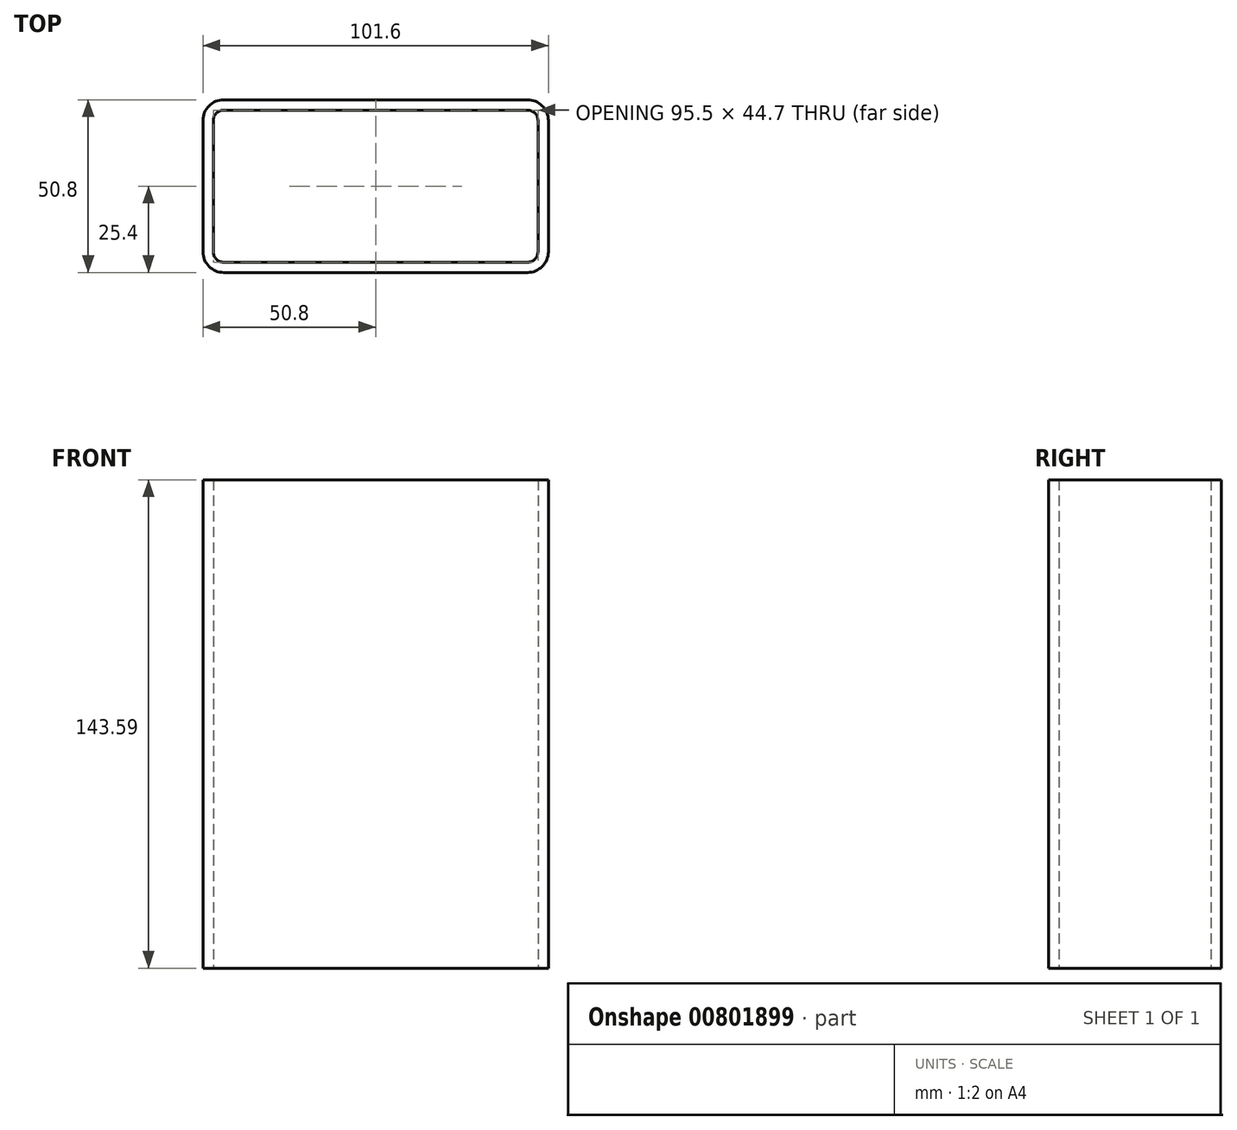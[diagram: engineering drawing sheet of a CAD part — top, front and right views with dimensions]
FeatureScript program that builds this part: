
annotation { "Feature Type Name" : "Feature", "Feature Type Description" : "" }
export const myFeature = defineFeature(function(context is Context, id is Id, definition is map)
    precondition{}
    {
        {
            var Q0;
            Q0=qCreatedBy(makeId("Top.planeOp"),FACE);
            var sketch = newSketch(context, id + "F0", { "sketchPlane" : qUnion([Q0])});
            skLineSegment(sketch, "E0.bottom", {"start": v(6.1, 0) * mm, "end": v(95.5, 0) * mm});
            skLineSegment(sketch, "E0.top", {"start": v(6.1, 50.8) * mm, "end": v(95.5, 50.8) * mm});
            skLineSegment(sketch, "E0.left", {"start": v(0, 6.1) * mm, "end": v(0, 44.7) * mm});
            skLineSegment(sketch, "E0.right", {"start": v(101.6, 6.1) * mm, "end": v(101.6, 44.7) * mm});
            skLineSegment(sketch, "E1.bottom", {"start": v(6.1, 47.75) * mm, "end": v(95.5, 47.75) * mm});
            skLineSegment(sketch, "E1.top", {"start": v(6.1, 3.05) * mm, "end": v(95.5, 3.05) * mm});
            skLineSegment(sketch, "E1.left", {"start": v(3.05, 44.7) * mm, "end": v(3.05, 6.1) * mm});
            skLineSegment(sketch, "E1.right", {"start": v(98.55, 44.7) * mm, "end": v(98.55, 6.1) * mm});
            skPoint(sketch, "E2.visualSharp", {"position": v(3.05, 47.75) * mm});
            skArc(sketch, "E2.filletArc", {"start": v(6.1, 47.75) * mm, "mid": v(3.94, 46.86) * mm, "end": v(3.05, 44.7) * mm});
            skPoint(sketch, "E3.visualSharp", {"position": v(98.55, 47.75) * mm});
            skArc(sketch, "E3.filletArc", {"start": v(98.55, 44.7) * mm, "mid": v(97.66, 46.86) * mm, "end": v(95.5, 47.75) * mm});
            skPoint(sketch, "E4.visualSharp", {"position": v(98.55, 3.05) * mm});
            skArc(sketch, "E4.filletArc", {"start": v(95.5, 3.05) * mm, "mid": v(97.66, 3.94) * mm, "end": v(98.55, 6.1) * mm});
            skPoint(sketch, "E5.visualSharp", {"position": v(3.05, 3.05) * mm});
            skArc(sketch, "E5.filletArc", {"start": v(3.05, 6.1) * mm, "mid": v(3.94, 3.94) * mm, "end": v(6.1, 3.05) * mm});
            skPoint(sketch, "E6.visualSharp", {"position": v(0, 50.8) * mm});
            skArc(sketch, "E6.filletArc", {"start": v(6.1, 50.8) * mm, "mid": v(1.79, 49.01) * mm, "end": v(0, 44.7) * mm});
            skPoint(sketch, "E7.visualSharp", {"position": v(101.6, 50.8) * mm});
            skArc(sketch, "E7.filletArc", {"start": v(101.6, 44.7) * mm, "mid": v(99.81, 49.01) * mm, "end": v(95.5, 50.8) * mm});
            skPoint(sketch, "E8.visualSharp", {"position": v(101.6, 0) * mm});
            skArc(sketch, "E8.filletArc", {"start": v(95.5, 0) * mm, "mid": v(99.81, 1.79) * mm, "end": v(101.6, 6.1) * mm});
            skPoint(sketch, "E9.visualSharp", {"position": v(0, 0) * mm});
            skArc(sketch, "E9.filletArc", {"start": v(0, 6.1) * mm, "mid": v(1.79, 1.79) * mm, "end": v(6.1, 0) * mm});
            skSolve(sketch);
        }
        {
            var Q0;
            Q0=qSketchRegion(id+"F0",true);
            extrude(context, id + "F1", {"entities" : qUnion([Q0]), "depth" : 143.6 * mm, "offsetDistance" : 25 * mm});
        }
    });
